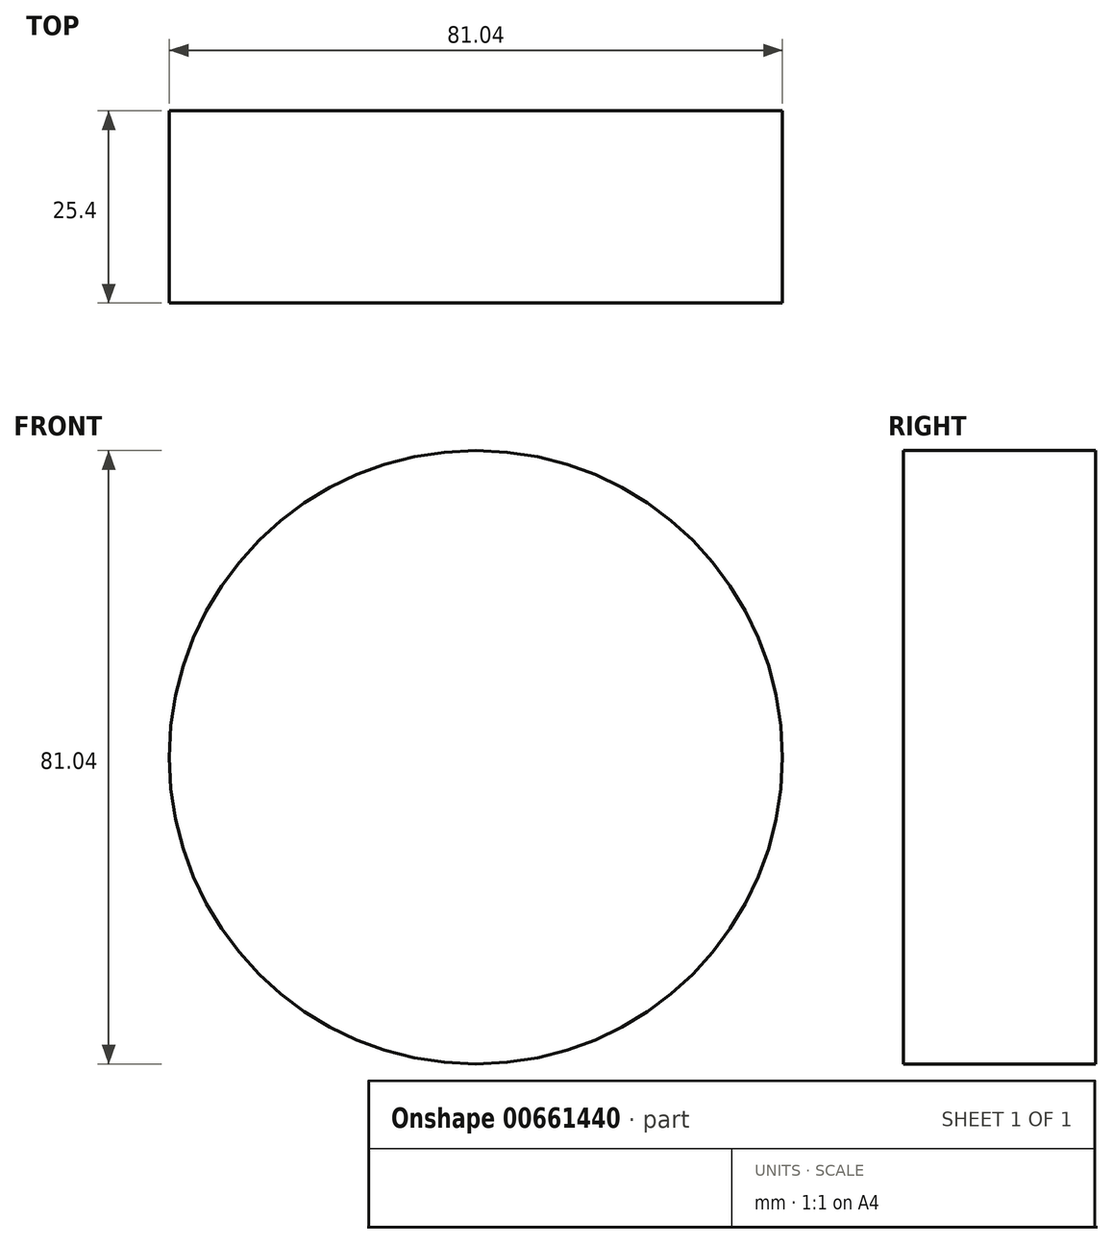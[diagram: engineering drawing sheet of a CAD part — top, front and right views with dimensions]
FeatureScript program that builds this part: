
annotation { "Feature Type Name" : "Feature", "Feature Type Description" : "" }
export const myFeature = defineFeature(function(context is Context, id is Id, definition is map)
    precondition{}
    {
        {
            var Q0;
            Q0=qCreatedBy(makeId("Front.planeOp"),FACE);
            var sketch = newSketch(context, id + "F0", { "sketchPlane" : qUnion([Q0])});
            skCircle(sketch, "E0", {"center": v(0, 0) * mm, "radius": 40.52 * mm});
            skSolve(sketch);
        }
        {
            var Q0;
            Q0 = qSketchRegion(id + "F0", true);
            extrude(context, id + "F1", {"entities" : qUnion([Q0]), "depth" : 25.4 * mm, "offsetDistance" : 25.4 * mm});
        }
    });
